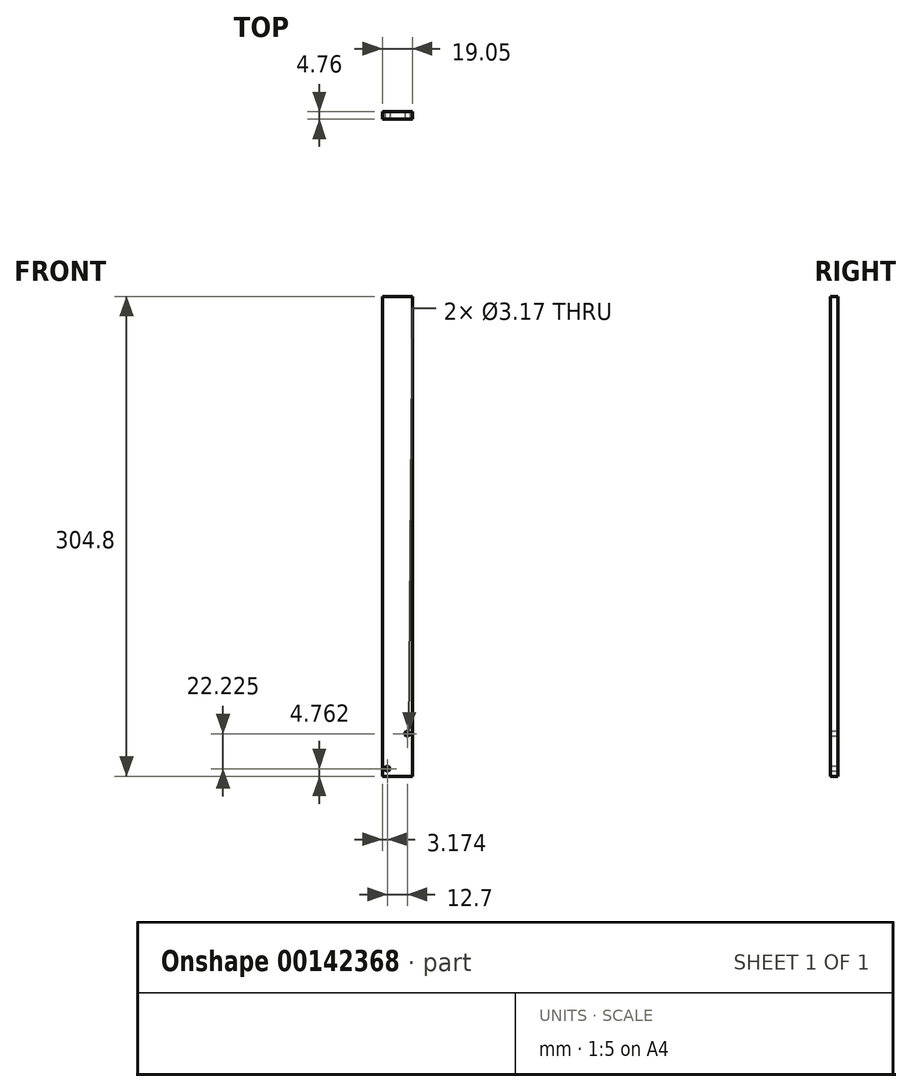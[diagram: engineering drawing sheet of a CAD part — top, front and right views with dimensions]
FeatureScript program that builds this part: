
annotation { "Feature Type Name" : "Feature", "Feature Type Description" : "" }
export const myFeature = defineFeature(function(context is Context, id is Id, definition is map)
    precondition{}
    {
        {
            var Q0;
            Q0=qCreatedBy(makeId("Front.planeOp"),FACE);
            var sketch = newSketch(context, id + "F0", { "sketchPlane" : qUnion([Q0])});
            skLineSegment(sketch, "E0.bottom", {"start": v(-10.4, -57.15) * mm, "end": v(8.66, -57.15) * mm});
            skLineSegment(sketch, "E0.top", {"start": v(-10.4, 247.65) * mm, "end": v(8.66, 247.65) * mm});
            skLineSegment(sketch, "E0.left", {"start": v(-10.4, -57.15) * mm, "end": v(-10.4, 247.65) * mm});
            skLineSegment(sketch, "E0.right", {"start": v(8.66, -57.15) * mm, "end": v(8.66, 247.65) * mm});
            skSolve(sketch);
        }
        {
            var Q0;
            Q0 = qSketchRegion(id + "F0", true);
            extrude(context, id + "F1", {"entities" : qUnion([Q0]), "depth" : 4.76 * mm});
        }
        {
            var Q0;
            Q0=makeQuery(id+"F1.opExtrude","CAP_FACE",FACE,{"disambiguationData":[OSD([sQuery(id+"F0.wireOp",EDGE,"E0.bottom"),sQuery(id+"F0.wireOp",EDGE,"E0.top"),sQuery(id+"F0.wireOp",EDGE,"E0.left"),sQuery(id+"F0.wireOp",EDGE,"E0.right")])],"isStart":false});
            var sketch = newSketch(context, id + "F2", { "sketchPlane" : qUnion([Q0])});
            skCircle(sketch, "E1", {"center": v(5.48, -30.16) * mm, "radius": 1.59 * mm});
            skCircle(sketch, "E2", {"center": v(-7.22, -52.39) * mm, "radius": 1.59 * mm});
            skSolve(sketch);
        }
        {
            var Q0;
            Q0 = qSketchRegion(id + "F2", true);
            var Q1;
            Q1=makeQuery(id+"F1.opExtrude","CAP_FACE",FACE,{"disambiguationData":[OSD([sQuery(id+"F0.wireOp",EDGE,"E0.bottom"),sQuery(id+"F0.wireOp",EDGE,"E0.top"),sQuery(id+"F0.wireOp",EDGE,"E0.left"),sQuery(id+"F0.wireOp",EDGE,"E0.right")])],"isStart":true});
            extrude(context, id + "F3", {"entities" : qUnion([Q0]), "operationType" : NewBodyOperationType.REMOVE, "endBound" : BoundingType.UP_TO_SURFACE, "oppositeDirection" : true, "endBoundEntityFace" : qUnion([Q1]), "depth" : 25.4 * mm});
        }
    });
